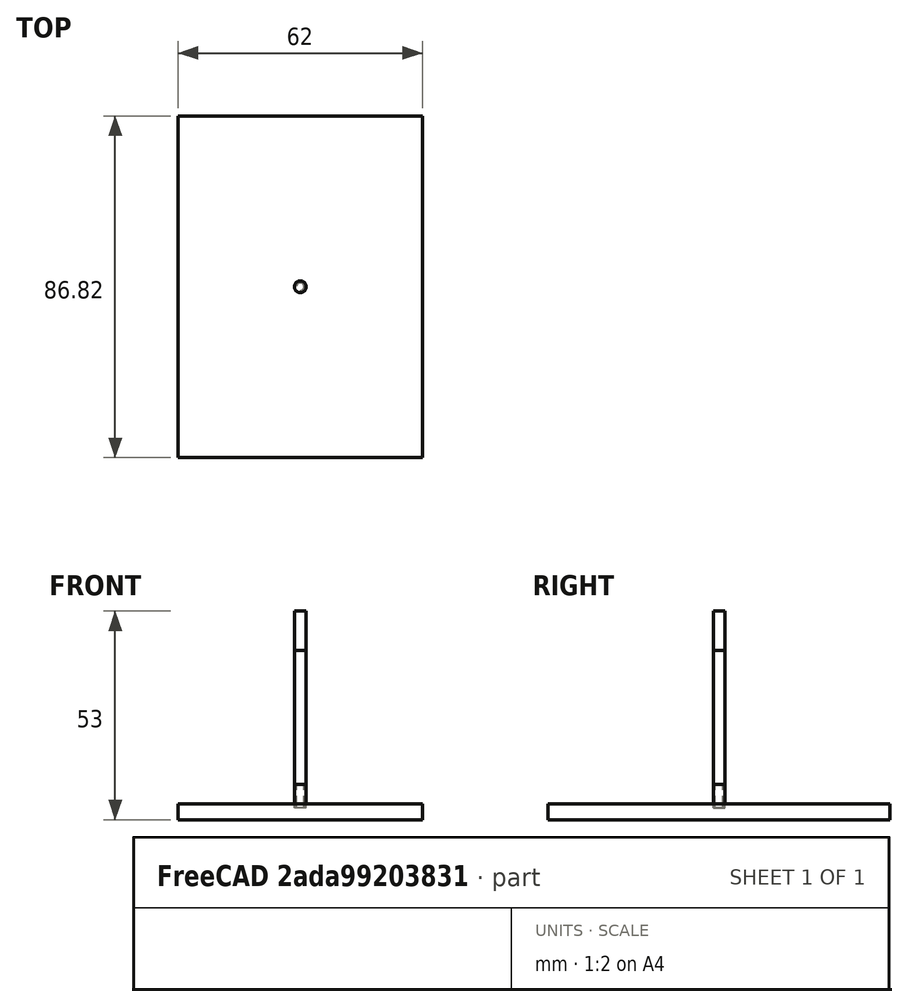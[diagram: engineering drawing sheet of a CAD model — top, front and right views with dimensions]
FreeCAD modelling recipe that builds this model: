
FCSTD DOCUMENT  (FreeCAD 1.0R39109 (Git))
Label: BackFastening_2
License: All rights reserved
LicenseURL: http://en.wikipedia.org/wiki/All_rights_reserved
objects: Path::FeaturePython×5, Part::FeaturePython×4, App::DocumentObjectGroup×3, Part::Feature×1, App::FeaturePython×1
note: 7 computed .brp shape members not serialized (recipe doc carries the construction recipe); baked Part::Feature solids carry a one-line shape summary decoded from their .brp

FEATURE [Part::Feature] Solid  label="BackFastening_2_model"
  shape: bbox 54 x 78.82 x 3 mm, 45 faces (baked)
FEATURE [App::FeaturePython] SetupSheet  # Path/CAM operation (typed FeaturePython)
  ClearanceHeightExpression = OpStockZMax+SetupSheet.ClearanceHeightOffset
  ClearanceHeightOffset = 5
  CoolantMode = 0
  CoolantModes = None | Flood | Mist
  FinalDepthExpression = OpFinalDepth
  HorizRapid = 0
  SafeHeightExpression = OpStockZMax+SetupSheet.SafeHeightOffset
  SafeHeightOffset = 3
  StartDepthExpression = OpStartDepth
  StepDownExpression = OpToolDiameter
  VertRapid = 0
FEATURE [Part::FeaturePython] Clone  label="Model-BackFastening_2_model"  # Draft clone (typed FeaturePython)
  AttacherType = Attacher::AttachEngine3D
  Fuse = false
  Objects = -> [Solid]
  PathResource = Model
  Placement = pos=(159.925,-145.921,-3) rot=(0,0,1;0rad)
  Scale = (1,1,1)
FEATURE [App::DocumentObjectGroup] Model
  Group = -> [Clone]
FEATURE [Part::FeaturePython] ToolBit001  label="3mm Endmill"  # Path/CAM toolbit (typed FeaturePython)
  BitPropertyNames = Chipload | CuttingEdgeHeight | Diameter | Flutes | Length | Material | ShankDiameter | SpindleDirection
  BitShape = <path>
  Chipload = 0
  CuttingEdgeHeight = 15
  Diameter = 3
  File = <path>
  Flutes = 0
  Length = 50
  Material = 0
  ShankDiameter = 3
  ShapeName = endmill
  SpindleDirection = 0
FEATURE [Path::FeaturePython] _mm_Endmill  label="3mm Endmill001"  # Path/CAM operation (typed FeaturePython)
  HorizFeed = 6.66667
  HorizRapid = 0
  SpindleDir = 0
  SpindleSpeed = 10000
  Tool = -> ToolBit001
  ToolNumber = 2
  VertFeed = 6.66667
  VertRapid = 0
  expr: HorizRapid = SetupSheet.HorizRapid
  expr: VertRapid = SetupSheet.VertRapid
FEATURE [Part::FeaturePython] Stock001  # WARN: FeaturePython — macro-defined, semantics opaque (R4)
  Base = -> Model
  ExtXneg = 4
  ExtXpos = 4
  ExtYneg = 4
  ExtYpos = 4
  ExtZneg = 0
  ExtZpos = 1
  Placement = pos=(-27,-39.4093,-3) rot=(0,0,1;0rad)
  StockType = FromBase
FEATURE [Part::FeaturePython] ToolBit  label="2mm Endmill"  # Path/CAM toolbit (typed FeaturePython)
  BitPropertyNames = Chipload | CuttingEdgeHeight | Diameter | Flutes | Length | Material | ShankDiameter | SpindleDirection
  BitShape = <path>
  Chipload = 0
  CuttingEdgeHeight = 6
  Diameter = 2
  File = <path>
  Flutes = 0
  Length = 40
  Material = 0
  ShankDiameter = 3
  ShapeName = endmill
  SpindleDirection = 0
FEATURE [Path::FeaturePython] _mm_Endmill001  label="2mm Endmill001"  # Path/CAM operation (typed FeaturePython)
  HorizFeed = 6.66667
  HorizRapid = 0
  SpindleDir = 0
  SpindleSpeed = 10000
  Tool = -> ToolBit
  ToolNumber = 3
  VertFeed = 6.66667
  VertRapid = 0
  expr: HorizRapid = SetupSheet.HorizRapid
  expr: VertRapid = SetupSheet.VertRapid
FEATURE [App::DocumentObjectGroup] Tools
  Group = -> [_mm_Endmill,_mm_Endmill001]
FEATURE [Path::FeaturePython] Adaptive  label="CutHole"  # Path/CAM operation (typed FeaturePython)
  Active = true
  Base = -> [Clone]
  ClearanceHeight = 6
  CoolantMode = 0
  CycleTime = 00:09:25
  ExtensionCorners = true
  ExtensionLengthDefault = 1
  FinalDepth = -3
  FinishDepth = 0
  FinishingProfile = true
  ForceInsideOut = false
  HelixAngle = 5
  HelixConeAngle = 0
  HelixDiameterLimit = 0.5
  KeepToolDownRatio = 3
  LiftDistance = 0
  OpFinalDepth = -3
  OpStartDepth = 1
  OpStockZMax = 1
  OpStockZMin = -3
  OpToolDiameter = 2
  OperationType = 0
  SafeHeight = 4
  Side = 1
  StartDepth = 1
  StepDown = 4
  StepOver = 10
  StockToLeave = 0
  StopProcessing = false
  Stopped = false
  Tolerance = 0.1
  ToolController = -> _mm_Endmill001
  UseHelixArcs = false
  UseOutline = false
  expr: ClearanceHeight = OpStockZMax + SetupSheet.ClearanceHeightOffset
  expr: ExtensionLengthDefault = OpToolDiameter / 2
  expr: FinalDepth = OpFinalDepth
  expr: SafeHeight = OpStockZMax + SetupSheet.SafeHeightOffset
  expr: StartDepth = OpStartDepth
  expr: StepDown = OpToolDiameter * 2
FEATURE [Path::FeaturePython] Adaptive001  label="OutCut"  # Path/CAM operation (typed FeaturePython)
  Active = true
  Base = -> [Clone]
  ClearanceHeight = 6
  CoolantMode = 0
  CycleTime = 00:18:18
  ExtensionCorners = true
  ExtensionLengthDefault = 1
  FinalDepth = -3
  FinishDepth = 0
  FinishingProfile = true
  ForceInsideOut = false
  HelixAngle = 5
  HelixConeAngle = 0
  HelixDiameterLimit = 1
  KeepToolDownRatio = 3
  LiftDistance = 0
  OpFinalDepth = -3
  OpStartDepth = 1
  OpStockZMax = 1
  OpStockZMin = -3
  OpToolDiameter = 2
  OperationType = 1
  SafeHeight = 4
  Side = 0
  StartDepth = 1
  StepDown = 4
  StepOver = 10
  StockToLeave = 0
  StopProcessing = false
  Stopped = false
  Tolerance = 0.1
  ToolController = -> _mm_Endmill001
  UseHelixArcs = false
  UseOutline = false
  expr: ClearanceHeight = OpStockZMax + SetupSheet.ClearanceHeightOffset
  expr: ExtensionLengthDefault = OpToolDiameter / 2
  expr: FinalDepth = OpFinalDepth
  expr: SafeHeight = OpStockZMax + SetupSheet.SafeHeightOffset
  expr: StartDepth = OpStartDepth
  expr: StepDown = OpToolDiameter * 2
FEATURE [App::DocumentObjectGroup] Operations
  Group = -> [Adaptive,Adaptive001]
FEATURE [Path::FeaturePython] Job  # Path/CAM operation (typed FeaturePython)
  CycleTime = 00:27:43
  Fixtures = G54
  GeometryTolerance = 0.01
  JobType = 0
  Model = -> Model
  Operations = -> Operations
  OrderOutputBy = 0
  PostProcessor = 11
  PostProcessorArgs = --bcnc
  PostProcessorOutputFile = %D\%d_OutCut
  SetupSheet = -> SetupSheet
  SplitOutput = false
  Stock = -> Stock001
  Tools = -> Tools
note: 4 file-system paths scrubbed to <path> (originals preserved in the JSON sidecar)
